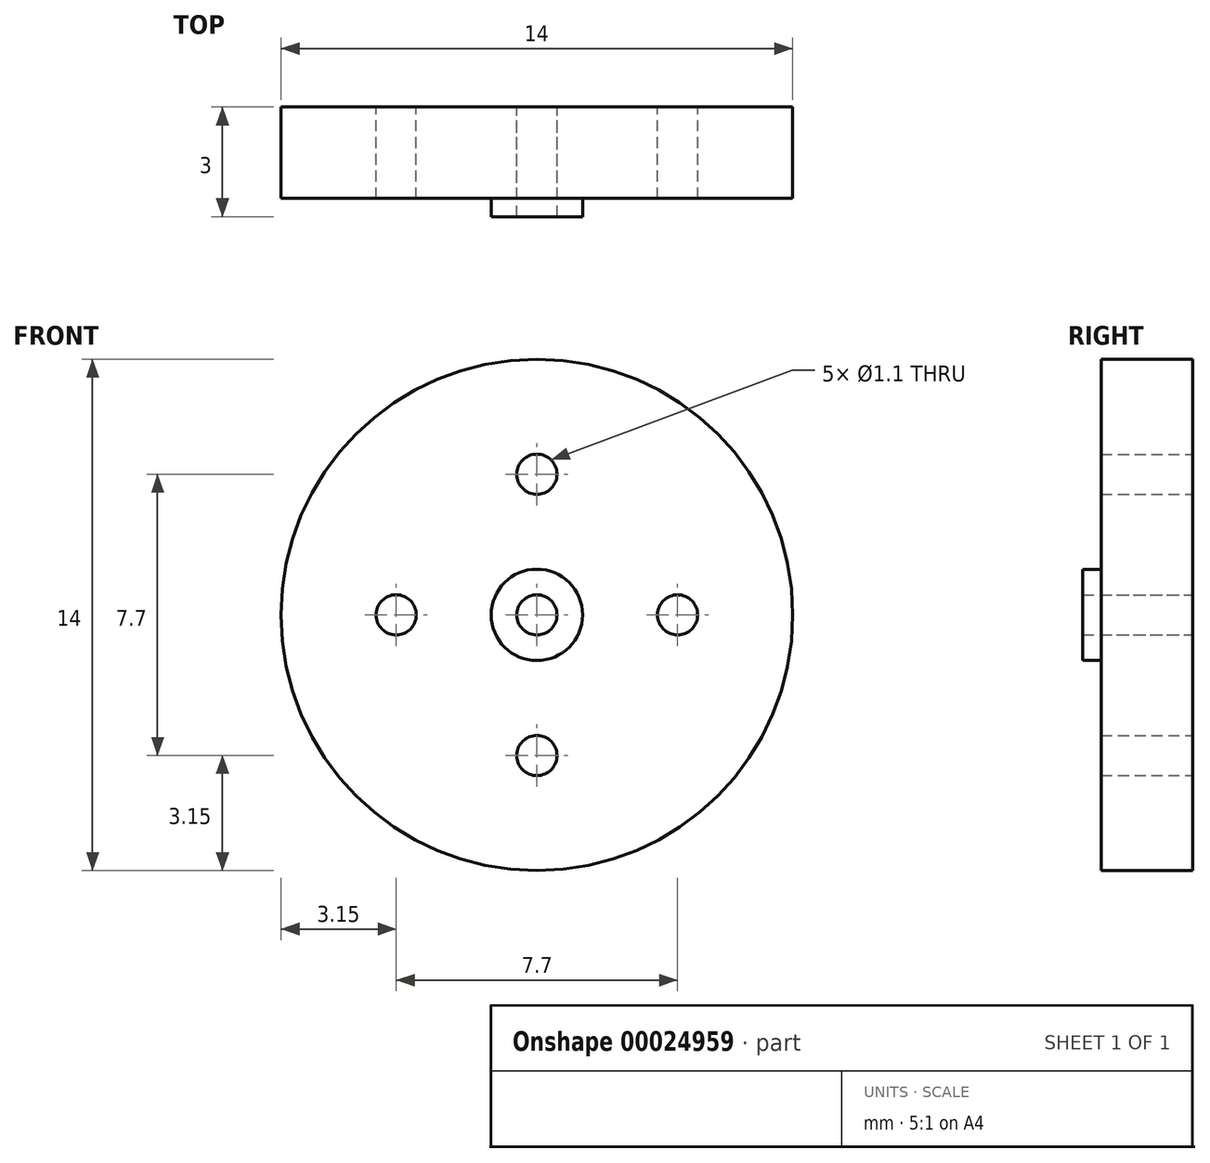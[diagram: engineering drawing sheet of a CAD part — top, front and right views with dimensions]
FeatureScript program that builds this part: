
annotation { "Feature Type Name" : "Feature", "Feature Type Description" : "" }
export const myFeature = defineFeature(function(context is Context, id is Id, definition is map)
    precondition{}
    {
        {
            var Q0;
            Q0=qCreatedBy(makeId("Front.planeOp"),FACE);
            var sketch = newSketch(context, id + "F0", { "sketchPlane" : qUnion([Q0])});
            skCircle(sketch, "E0", {"center": v(0, 0) * mm, "radius": 7 * mm});
            skCircle(sketch, "E1", {"center": v(0, 0) * mm, "radius": 1.25 * mm});
            skCircle(sketch, "E2", {"center": v(0, 0) * mm, "radius": 0.55 * mm});
            skCircle(sketch, "E3", {"center": v(0, 3.85) * mm, "radius": 0.55 * mm});
            skSolve(sketch);
        }
        {
            var Q0;
            Q0=makeQuery(id+"F0.imprint","IMPRINT",FACE,{"disambiguationData":[TD([[makeQuery(id+"F0.imprint","IMPRINT",EDGE,{"derivedFrom":sQuery(id+"F0.wireOp",EDGE,"E1")}),1.0]])]});
            extrude(context, id + "F1", {"entities" : qUnion([Q0]), "depth" : 3 * mm});
        }
        {
            var Q0;
            Q0=makeQuery(id+"F0.imprint","IMPRINT",FACE,{"disambiguationData":[TD([[makeQuery(id+"F0.imprint","IMPRINT",EDGE,{"derivedFrom":sQuery(id+"F0.wireOp",EDGE,"E0")}),1.0]])]});
            extrude(context, id + "F2", {"entities" : qUnion([Q0]), "operationType" : NewBodyOperationType.ADD, "depth" : 2.5 * mm});
        }
        {
            var Q0;
            Q0=makeQuery(id+"F2.opExtrude","SWEPT_FACE",FACE,{"disambiguationData":[OSD([sQuery(id+"F0.wireOp",EDGE,"E3")])]});
            var Q1;
            Q1=sQuery(id+"F0.wireOp",EDGE,"E0");
            circularPattern(context, id + "F3", {"faces" : qUnion([Q0]), "axis" : qUnion([Q1]), "angle" : 90 * degree, "instanceCount" : round(4), "patternType" : PatternType.FACE});
        }
    });
